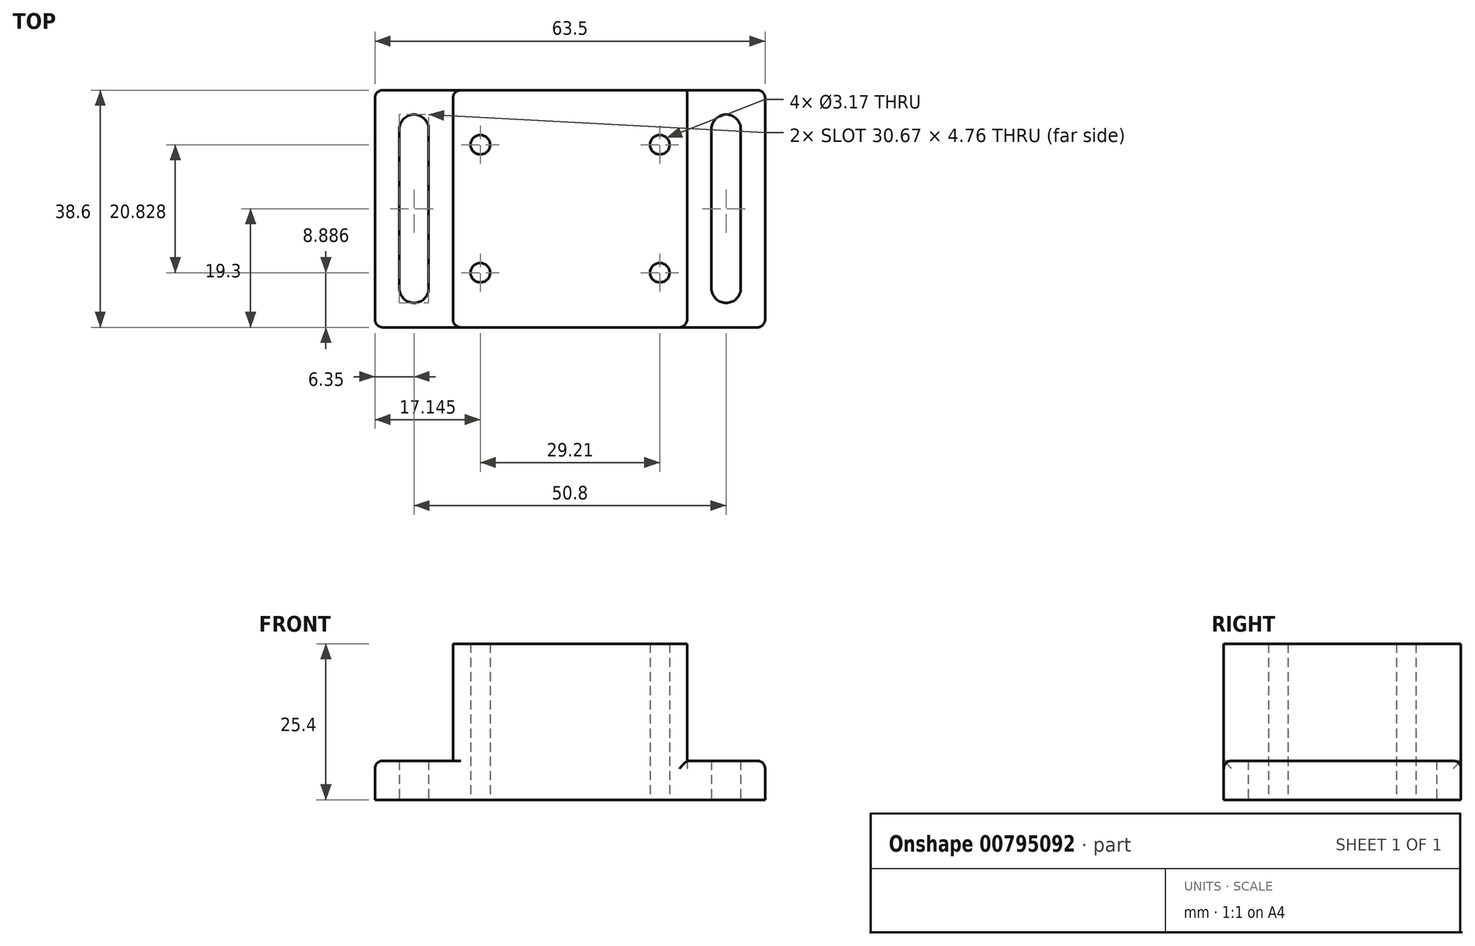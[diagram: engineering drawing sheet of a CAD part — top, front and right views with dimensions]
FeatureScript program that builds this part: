
annotation { "Feature Type Name" : "Feature", "Feature Type Description" : "" }
export const myFeature = defineFeature(function(context is Context, id is Id, definition is map)
    precondition{}
    {
        {
            var Q0;
            Q0=qCreatedBy(makeId("Top.planeOp"),FACE);
            var sketch = newSketch(context, id + "F0", { "sketchPlane" : qUnion([Q0])});
            skLineSegment(sketch, "E0", {"start": v(19.05, 19.3) * mm, "end": v(-19.05, 19.3) * mm});
            skLineSegment(sketch, "E1", {"start": v(-19.05, 19.3) * mm, "end": v(-19.05, -19.3) * mm});
            skLineSegment(sketch, "E2", {"start": v(-19.05, -19.3) * mm, "end": v(19.05, -19.3) * mm});
            skLineSegment(sketch, "E3", {"start": v(19.05, -19.3) * mm, "end": v(19.05, 19.3) * mm});
            skLineSegment(sketch, "E4", {"start": v(0, 0) * mm, "end": v(19.05, 0) * mm});
            skLineSegment(sketch, "E5", {"start": v(19.05, 19.3) * mm, "end": v(31.75, 19.3) * mm});
            skLineSegment(sketch, "E6", {"start": v(31.75, 19.3) * mm, "end": v(31.75, -19.3) * mm});
            skLineSegment(sketch, "E7", {"start": v(31.75, -19.3) * mm, "end": v(19.05, -19.3) * mm});
            skLineSegment(sketch, "E8", {"start": v(-19.05, 19.3) * mm, "end": v(-31.75, 19.3) * mm});
            skLineSegment(sketch, "E9", {"start": v(-31.75, 19.3) * mm, "end": v(-31.75, -19.3) * mm});
            skLineSegment(sketch, "E10", {"start": v(-31.75, -19.3) * mm, "end": v(-19.05, -19.3) * mm});
            skLineSegment(sketch, "E11", {"start": v(25.4, -19.3) * mm, "end": v(25.4, -12.95) * mm});
            skCircle(sketch, "E12", {"center": v(25.4, 12.95) * mm, "radius": 2.38 * mm});
            skCircle(sketch, "E13", {"center": v(25.4, -12.95) * mm, "radius": 2.38 * mm});
            skLineSegment(sketch, "E14", {"start": v(27.78, 12.95) * mm, "end": v(27.78, -12.95) * mm});
            skLineSegment(sketch, "E15", {"start": v(23.02, -12.95) * mm, "end": v(23.02, 12.95) * mm});
            skCircle(sketch, "E16", {"center": v(-25.4, 12.95) * mm, "radius": 2.38 * mm});
            skCircle(sketch, "E17", {"center": v(-25.4, -12.95) * mm, "radius": 2.38 * mm});
            skLineSegment(sketch, "E18", {"start": v(-23.02, 12.95) * mm, "end": v(-23.02, -12.95) * mm});
            skLineSegment(sketch, "E19", {"start": v(-27.78, -12.95) * mm, "end": v(-27.78, 12.95) * mm});
            skCircle(sketch, "E20", {"center": v(-14.6, -10.41) * mm, "radius": 1.59 * mm});
            skCircle(sketch, "E21", {"center": v(-14.6, 10.41) * mm, "radius": 1.59 * mm});
            skCircle(sketch, "E22", {"center": v(14.6, 10.41) * mm, "radius": 1.59 * mm});
            skCircle(sketch, "E23", {"center": v(14.6, -10.41) * mm, "radius": 1.59 * mm});
            skSolve(sketch);
        }
        {
            var Q0;
            {var subQ3=sQuery(id+"F0.wireOp",EDGE,"E0");Q0=makeQuery(id+"F0.imprint","IMPRINT",FACE,{"disambiguationData":[TD([[makeQuery(id+"F0.imprint","IMPRINT",EDGE,{"derivedFrom":subQ3}),1.0]])]});}
            extrude(context, id + "F1", {"entities" : qUnion([Q0]), "depth" : 25.4 * mm, "offsetDistance" : 25.4 * mm});
        }
        {
            var Q0;
            Q0=makeQuery(id+"F0.imprint","IMPRINT",FACE,{"disambiguationData":[TD([[makeQuery(id+"F0.imprint","IMPRINT",EDGE,{"derivedFrom":sQuery(id+"F0.wireOp",EDGE,"E1")}),-1.0]])]});
            var Q1;
            {var subQ11=sQuery(id+"F0.wireOp",EDGE,"E5");Q1=makeQuery(id+"F0.imprint","IMPRINT",FACE,{"disambiguationData":[TD([[makeQuery(id+"F0.imprint","IMPRINT",EDGE,{"derivedFrom":subQ11}),-1.0]])]});}
            extrude(context, id + "F2", {"entities" : qUnion([Q0, Q1]), "operationType" : NewBodyOperationType.ADD, "depth" : 6.35 * mm, "offsetDistance" : 25.4 * mm});
        }
        {
            var Q0;
            Q0=makeQuery(id+"F2.opExtrude","CAP_EDGE",EDGE,{"disambiguationData":[OSD([sQuery(id+"F0.wireOp",EDGE,"E1")])],"isStart":false});
            var Q1;
            Q1=makeQuery(id+"F1.opExtrude","SWEPT_EDGE",EDGE,{"disambiguationData":[OSD([sQuery(id+"F0.wireOp",EDGE,"E1"),sQuery(id+"F0.wireOp",EDGE,"E2"),sQuery(id+"F0.wireOp",EDGE,"E10")])]});
            var Q2;
            Q2=makeQuery(id+"F1.opExtrude","SWEPT_EDGE",EDGE,{"disambiguationData":[OSD([sQuery(id+"F0.wireOp",EDGE,"E0"),sQuery(id+"F0.wireOp",EDGE,"E1"),sQuery(id+"F0.wireOp",EDGE,"E8")])]});
            var Q3;
            Q3=makeQuery(id+"F2.opExtrude","CAP_EDGE",EDGE,{"disambiguationData":[OSD([sQuery(id+"F0.wireOp",EDGE,"E9")])],"isStart":false});
            var Q4;
            Q4=makeQuery(id+"F2.opExtrude","SWEPT_EDGE",EDGE,{"disambiguationData":[OSD([sQuery(id+"F0.wireOp",EDGE,"E9"),sQuery(id+"F0.wireOp",EDGE,"E10")])]});
            var Q5;
            Q5=makeQuery(id+"F2.opExtrude","SWEPT_EDGE",EDGE,{"disambiguationData":[OSD([sQuery(id+"F0.wireOp",EDGE,"E8"),sQuery(id+"F0.wireOp",EDGE,"E9")])]});
            var Q6;
            Q6=makeQuery(id+"F2.opExtrude","CAP_EDGE",EDGE,{"disambiguationData":[OSD([sQuery(id+"F0.wireOp",EDGE,"E7")])],"isStart":false});
            var Q7;
            Q7=makeQuery(id+"F1.opExtrude","SWEPT_EDGE",EDGE,{"disambiguationData":[OSD([sQuery(id+"F0.wireOp",EDGE,"E2"),sQuery(id+"F0.wireOp",EDGE,"E3"),sQuery(id+"F0.wireOp",EDGE,"E7")])]});
            var Q8;
            Q8=makeQuery(id+"F2.opExtrude","SWEPT_EDGE",EDGE,{"disambiguationData":[OSD([sQuery(id+"F0.wireOp",EDGE,"E6"),sQuery(id+"F0.wireOp",EDGE,"E7")])]});
            var Q9;
            Q9=makeQuery(id+"F2.opExtrude","CAP_EDGE",EDGE,{"disambiguationData":[OSD([sQuery(id+"F0.wireOp",EDGE,"E3")])],"isStart":false});
            var Q10;
            Q10=makeQuery(id+"F2.opExtrude","CAP_EDGE",EDGE,{"disambiguationData":[OSD([sQuery(id+"F0.wireOp",EDGE,"E6")])],"isStart":false});
            var Q11;
            Q11=makeQuery(id+"F2.opExtrude","SWEPT_EDGE",EDGE,{"disambiguationData":[OSD([sQuery(id+"F0.wireOp",EDGE,"E5"),sQuery(id+"F0.wireOp",EDGE,"E6")])]});
            var Q12;
            Q12=makeQuery(id+"F2.opExtrude","CAP_EDGE",EDGE,{"disambiguationData":[OSD([sQuery(id+"F0.wireOp",EDGE,"E5")])],"isStart":false});
            fillet(context, id + "F3", {"entities" : qUnion([Q0, Q1, Q2, Q3, Q4, Q5, Q6, Q7, Q8, Q9, Q10, Q11, Q12]), "radius" : 1.27 * mm, "tangentPropagation" : true, "allowEdgeOverflow" : false});
        }
    });
